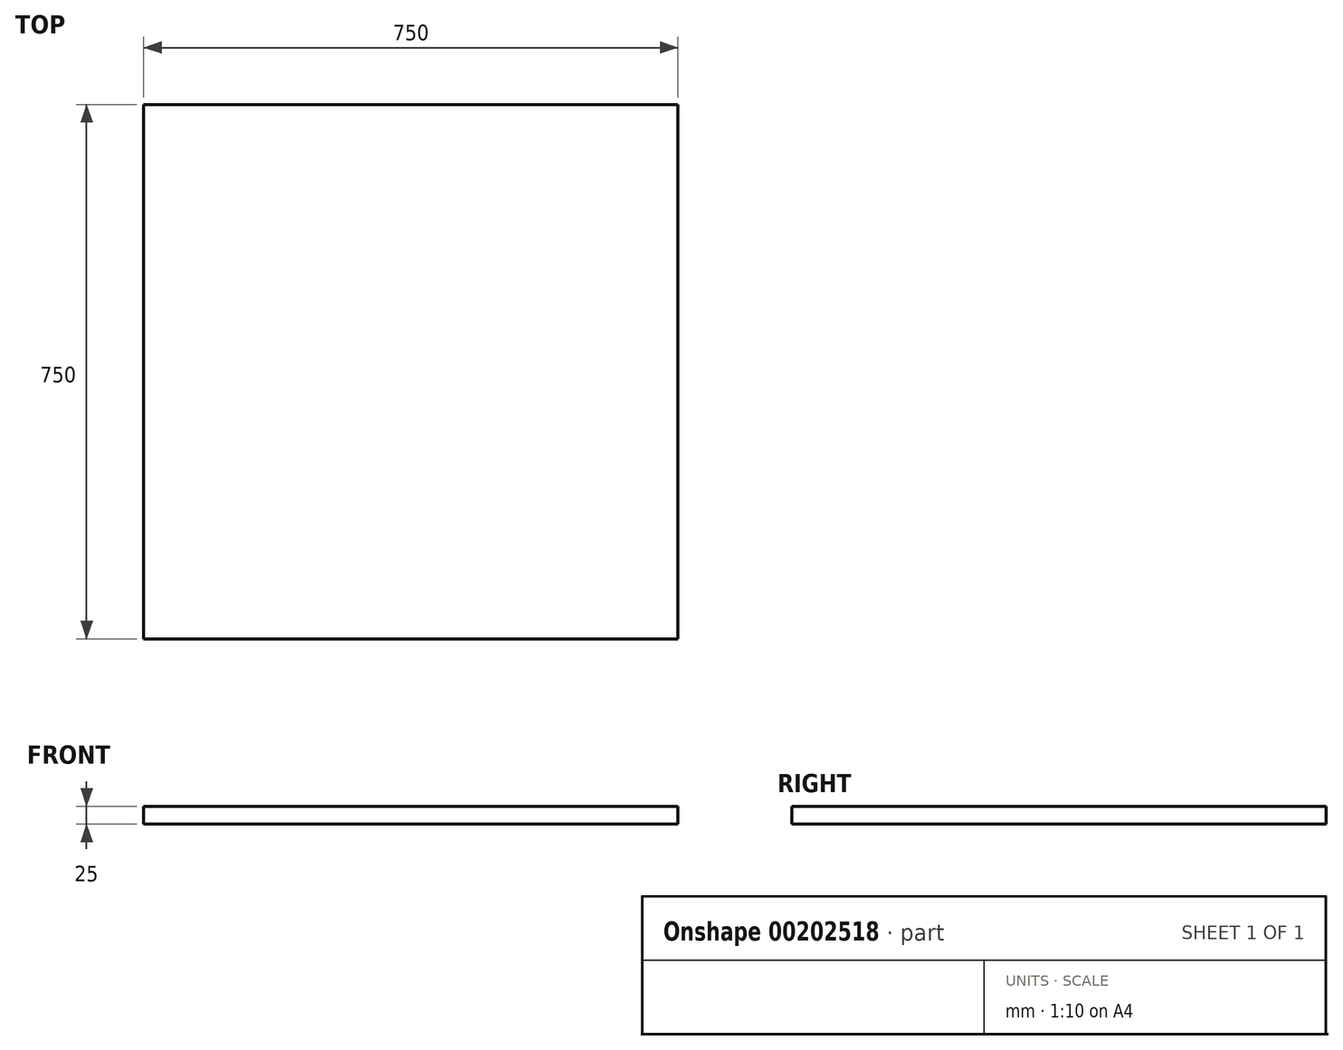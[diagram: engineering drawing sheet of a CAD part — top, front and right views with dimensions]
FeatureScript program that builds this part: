
annotation { "Feature Type Name" : "Feature", "Feature Type Description" : "" }
export const myFeature = defineFeature(function(context is Context, id is Id, definition is map)
    precondition{}
    {
        {
            var Q0;
            Q0=qCreatedBy(makeId("Top.planeOp"),FACE);
            var sketch = newSketch(context, id + "F0", { "sketchPlane" : qUnion([Q0])});
            skLineSegment(sketch, "E0.bottom", {"start": v(-375, -375) * mm, "end": v(375, -375) * mm});
            skLineSegment(sketch, "E0.top", {"start": v(-375, 375) * mm, "end": v(375, 375) * mm});
            skLineSegment(sketch, "E0.left", {"start": v(-375, -375) * mm, "end": v(-375, 375) * mm});
            skLineSegment(sketch, "E0.right", {"start": v(375, -375) * mm, "end": v(375, 375) * mm});
            skPoint(sketch, "E0.middle", {"position": v(0, 0) * mm});
            skSolve(sketch);
        }
        {
            var Q0;
            Q0=makeQuery(id+"F0.imprint","IMPRINT",FACE,{"disambiguationData":[TD([[makeQuery(id+"F0.imprint","IMPRINT",EDGE,{"derivedFrom":sQuery(id+"F0.wireOp",EDGE,"E0.bottom")}),1.0]])]});
            extrude(context, id + "F1", {"entities" : qUnion([Q0]), "depth" : 25 * mm});
        }
    });
